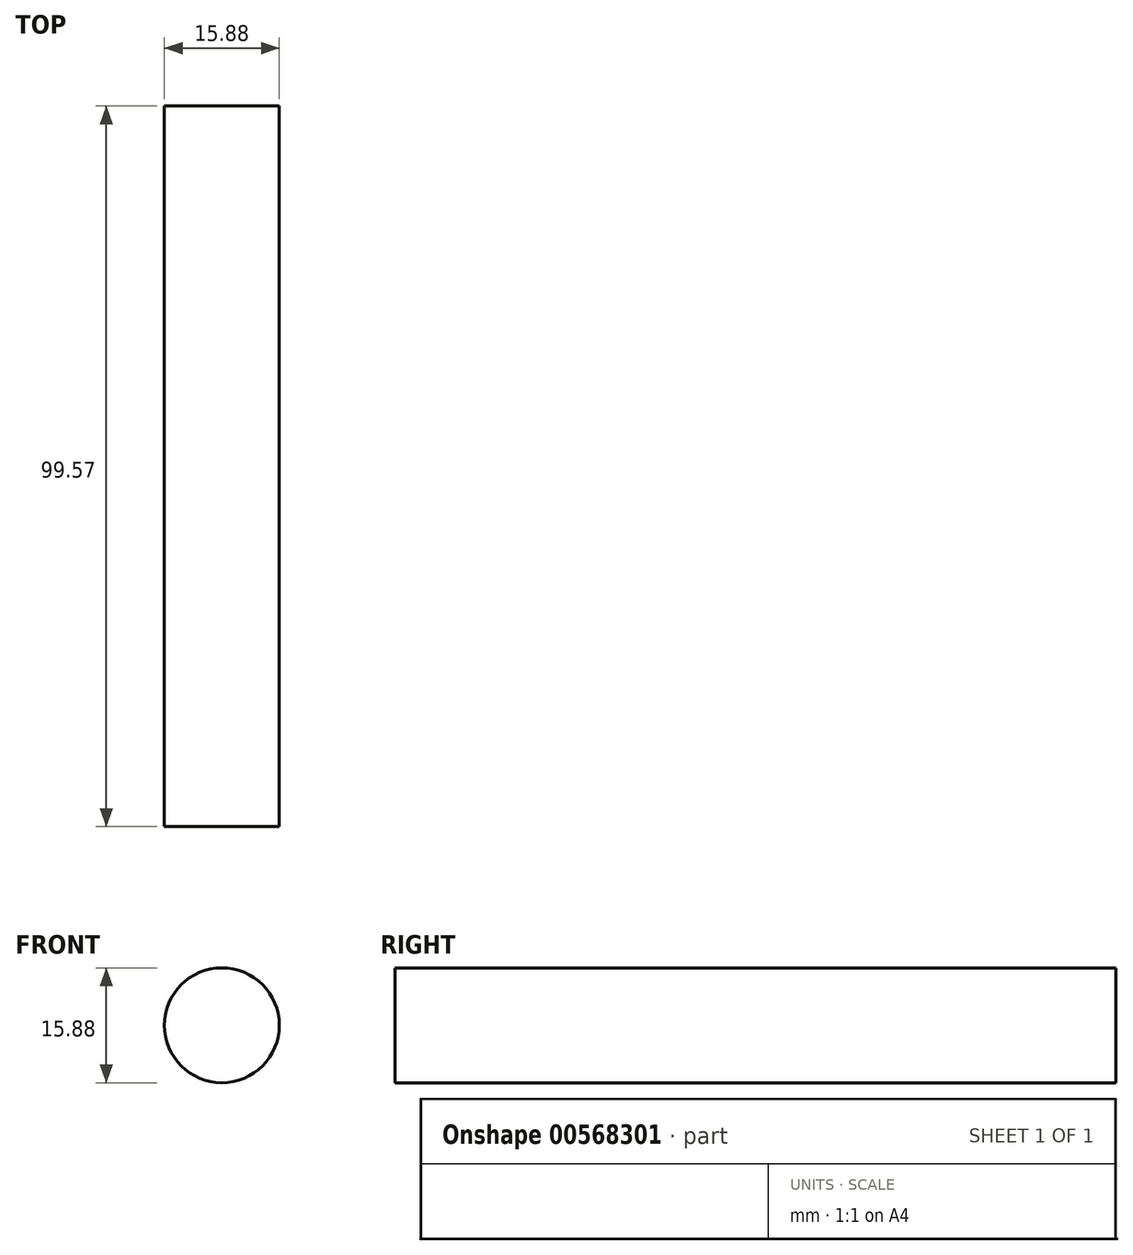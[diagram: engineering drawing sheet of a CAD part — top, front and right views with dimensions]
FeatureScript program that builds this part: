
annotation { "Feature Type Name" : "Feature", "Feature Type Description" : "" }
export const myFeature = defineFeature(function(context is Context, id is Id, definition is map)
    precondition{}
    {
        {
            var Q0;
            Q0=qCreatedBy(makeId("Front.planeOp"),FACE);
            var sketch = newSketch(context, id + "F0", { "sketchPlane" : qUnion([Q0])});
            skCircle(sketch, "E0", {"center": v(0, 0) * mm, "radius": 7.94 * mm});
            skSolve(sketch);
        }
        {
            var Q0;
            Q0=makeQuery(id+"F0.imprint","IMPRINT",FACE,{"disambiguationData":[TD([[makeQuery(id+"F0.imprint","IMPRINT",EDGE,{"derivedFrom":sQuery(id+"F0.wireOp",EDGE,"E0")}),1.0]])]});
            extrude(context, id + "F1", {"entities" : qUnion([Q0]), "depth" : 99.57 * mm, "offsetDistance" : 25.4 * mm});
        }
    });
